# Revit family: LB3S26337A75FTB-T.V3,A2FTB-T.V3
name_source: partatom
category: Plumbing Fixtures
units: mm (PartAtom-declared; Revit-internal decimal feet)

## family parameters
Always vertical = Yes
Cut with Voids When Loaded = No
OmniClass Number = 23.45.05.14.17
OmniClass Title = Showers
Part Type = Normal
Room Calculation Point = No
Round Connector Dimension = Use Diameter
Shared = No
Work Plane-Based = No

## types (4) — shared parameters
Assembly Code = D2010710
Keynote = 22 40 00.B3
Manufacturer = best bath
Type Comments = ADA Compliant
URL = http://www.bestbath.com
Unit Depth = 38 1/2"
Unit Width = 63"

## per-type parameters (varying)
| type | Description | Model | Threshold Height | Unit Height |
| LB3S26337A75FTB.V3 | Trench Drain, 12 x 18 Subway Tile, Beveled Threshold | LB3S26337A75FTB.V3 | 3/4" | 78 3/4" |
| LB3S26337A75FTT.V3 | Trench Drain, 12 x 18 Subway Tile, Traditional Threshold | LB3S26337A75FTT.V3 | 3/4" | 78 3/4" |
| LB3S26337A2FTT.V3 | Trench Drain, 12 x 18 Subway Tile, TraditionalThreshold | LB3S26337A2FTT.V3 | 2" | 80" |
| LB3S26337A2FTB.V3 | Trench Drain, 12 x 18 Subway Tile, Beveled Threshold | LB3S26337A75FTB.V3 | 3/4" | 78 3/4" |

## geometry (parser evidence)
native form markers: Blend x16, Sweep x7
no freeform markers — native parametric forms only
